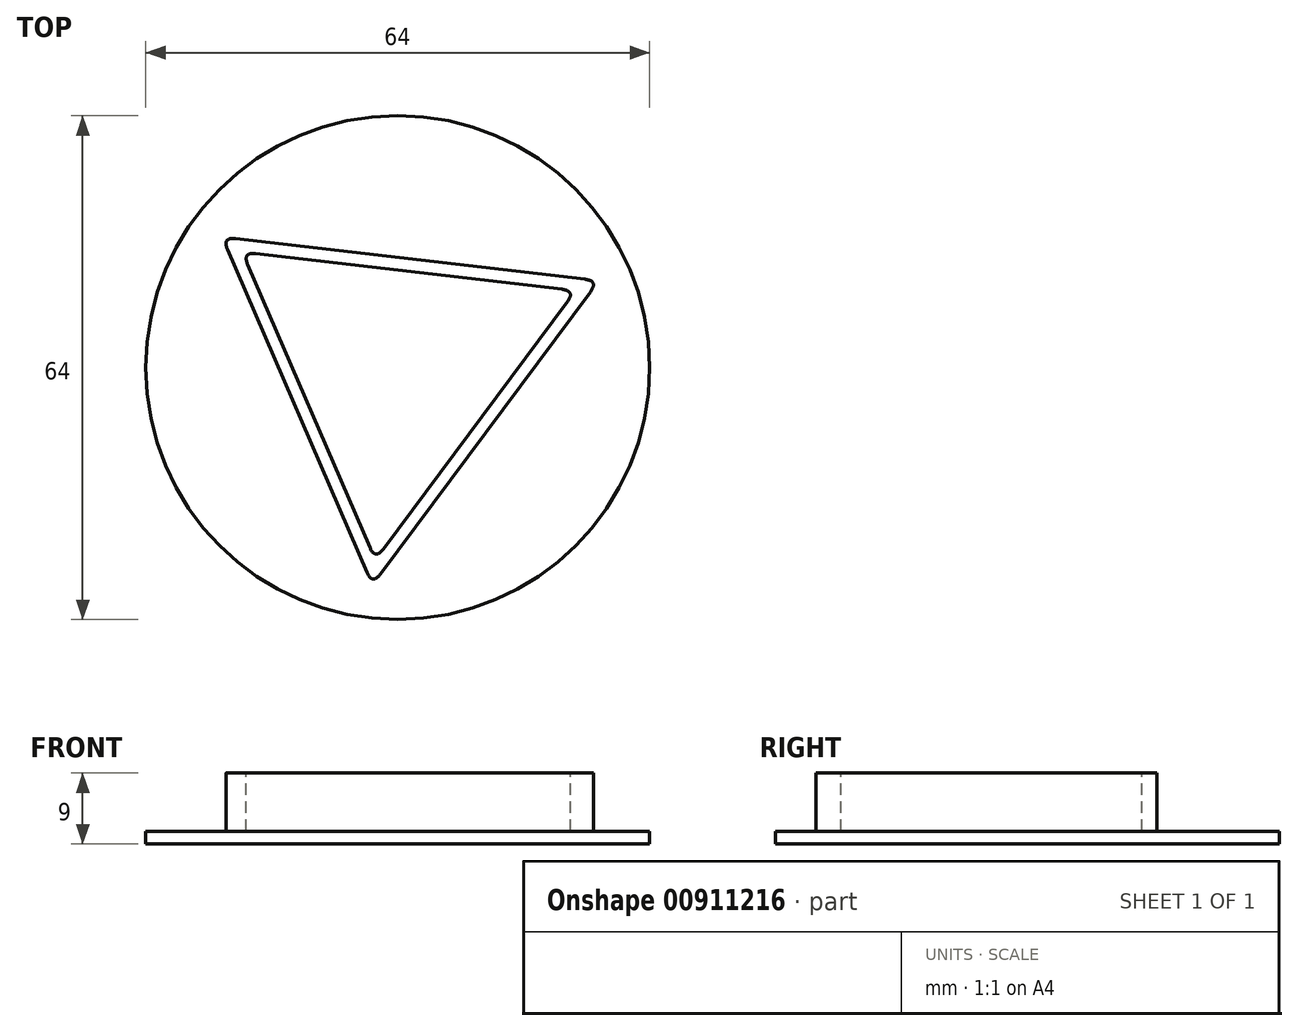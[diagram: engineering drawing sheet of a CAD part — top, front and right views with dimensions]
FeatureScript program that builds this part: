
annotation { "Feature Type Name" : "Feature", "Feature Type Description" : "" }
export const myFeature = defineFeature(function(context is Context, id is Id, definition is map)
    precondition{}
    {
        {
            var Q0;
            Q0=qCreatedBy(makeId("Top.planeOp"),FACE);
            var sketch = newSketch(context, id + "F0", { "sketchPlane" : qUnion([Q0])});
            skCircle(sketch, "E0.cCircle", {"center": v(0, 0) * mm, "radius": 27.8 * mm, "construction": true});
            skLineSegment(sketch, "E0.0", {"start": v(-22.3, 16.6) * mm, "end": v(25.52, 11.02) * mm});
            skLineSegment(sketch, "E0.1", {"start": v(25.52, 11.02) * mm, "end": v(-3.22, -27.61) * mm});
            skLineSegment(sketch, "E0.2", {"start": v(-3.22, -27.61) * mm, "end": v(-22.3, 16.6) * mm});
            skCircle(sketch, "E1", {"center": v(0, 0) * mm, "radius": 32 * mm});
            skLineSegment(sketch, "E2", {"start": v(-19.74, 14.69) * mm, "end": v(-2.85, -24.43) * mm});
            skLineSegment(sketch, "E3.trimOffspring", {"start": v(-19.74, 14.69) * mm, "end": v(22.59, 9.75) * mm});
            skLineSegment(sketch, "E4.trimOffspring", {"start": v(-2.85, -24.43) * mm, "end": v(22.59, 9.75) * mm});
            skSolve(sketch);
        }
        {
            var Q0;
            Q0=makeQuery(id+"F0.imprint","IMPRINT",FACE,{"disambiguationData":[TD([[makeQuery(id+"F0.imprint","IMPRINT",EDGE,{"derivedFrom":sQuery(id+"F0.wireOp",EDGE,"E0.0")}),1.0]])]});
            var Q1;
            Q1=makeQuery(id+"F0.imprint","IMPRINT",FACE,{"disambiguationData":[TD([[makeQuery(id+"F0.imprint","IMPRINT",EDGE,{"derivedFrom":sQuery(id+"F0.wireOp",EDGE,"E0.0")}),-1.0]])]});
            extrude(context, id + "F1", {"entities" : qUnion([Q0, Q1]), "depth" : 1.6 * mm, "offsetDistance" : 25 * mm});
        }
        {
            var Q0;
            Q0=makeQuery(id+"F0.imprint","IMPRINT",FACE,{"disambiguationData":[TD([[makeQuery(id+"F0.imprint","IMPRINT",EDGE,{"derivedFrom":sQuery(id+"F0.wireOp",EDGE,"E2")}),1.0]])]});
            extrude(context, id + "F2", {"entities" : qUnion([Q0]), "operationType" : NewBodyOperationType.ADD, "depth" : 1.6 * mm, "offsetDistance" : 25 * mm});
        }
        {
            var Q0;
            Q0=makeQuery(id+"F0.imprint","IMPRINT",FACE,{"disambiguationData":[TD([[makeQuery(id+"F0.imprint","IMPRINT",EDGE,{"derivedFrom":sQuery(id+"F0.wireOp",EDGE,"E0.0")}),-1.0]])]});
            var Q1;
            Q1=sQuery(id+"F0.wireOp",EDGE,"E0.1");
            var Q2;
            Q2=sQuery(id+"F0.wireOp",EDGE,"E4.trimOffspring");
            var Q3;
            Q3=sQuery(id+"F0.wireOp",EDGE,"E2");
            var Q4;
            Q4=sQuery(id+"F0.wireOp",EDGE,"E0.2");
            var Q5;
            Q5=sQuery(id+"F0.wireOp",EDGE,"E3.trimOffspring");
            var Q6;
            Q6=sQuery(id+"F0.wireOp",EDGE,"E0.0");
            extrude(context, id + "F3", {"entities" : qUnion([Q0]), "operationType" : NewBodyOperationType.ADD, "surfaceEntities" : qUnion([Q1, Q2, Q3, Q4, Q5, Q6]), "depth" : 9 * mm, "offsetDistance" : 25 * mm});
        }
        {
            var Q0;
            Q0=makeQuery(id+"F3.opExtrude","SWEPT_EDGE",EDGE,{"disambiguationData":[OSD([sQuery(id+"F0.wireOp",EDGE,"E0.1"),sQuery(id+"F0.wireOp",EDGE,"E0.2")])]});
            var Q1;
            Q1=makeQuery(id+"F3.opExtrude","SWEPT_EDGE",EDGE,{"disambiguationData":[OSD([sQuery(id+"F0.wireOp",EDGE,"E2"),sQuery(id+"F0.wireOp",EDGE,"E4.trimOffspring")])]});
            var Q2;
            Q2=makeQuery(id+"F3.opExtrude","SWEPT_EDGE",EDGE,{"disambiguationData":[OSD([sQuery(id+"F0.wireOp",EDGE,"E3.trimOffspring"),sQuery(id+"F0.wireOp",EDGE,"E4.trimOffspring")])]});
            var Q3;
            Q3=makeQuery(id+"F3.opExtrude","SWEPT_EDGE",EDGE,{"disambiguationData":[OSD([sQuery(id+"F0.wireOp",EDGE,"E0.0"),sQuery(id+"F0.wireOp",EDGE,"E0.1")])]});
            var Q4;
            Q4=makeQuery(id+"F3.opExtrude","SWEPT_EDGE",EDGE,{"disambiguationData":[OSD([sQuery(id+"F0.wireOp",EDGE,"E2"),sQuery(id+"F0.wireOp",EDGE,"E3.trimOffspring")])]});
            var Q5;
            Q5=makeQuery(id+"F3.opExtrude","SWEPT_EDGE",EDGE,{"disambiguationData":[OSD([sQuery(id+"F0.wireOp",EDGE,"E0.0"),sQuery(id+"F0.wireOp",EDGE,"E0.2")])]});
            fillet(context, id + "F4", {"entities" : qUnion([Q0, Q1, Q2, Q3, Q4, Q5]), "radius" : 1 * mm, "tangentPropagation" : true, "rho" : 0.5, "crossSection" : FilletCrossSection.CONIC, "allowEdgeOverflow" : false});
        }
    });
